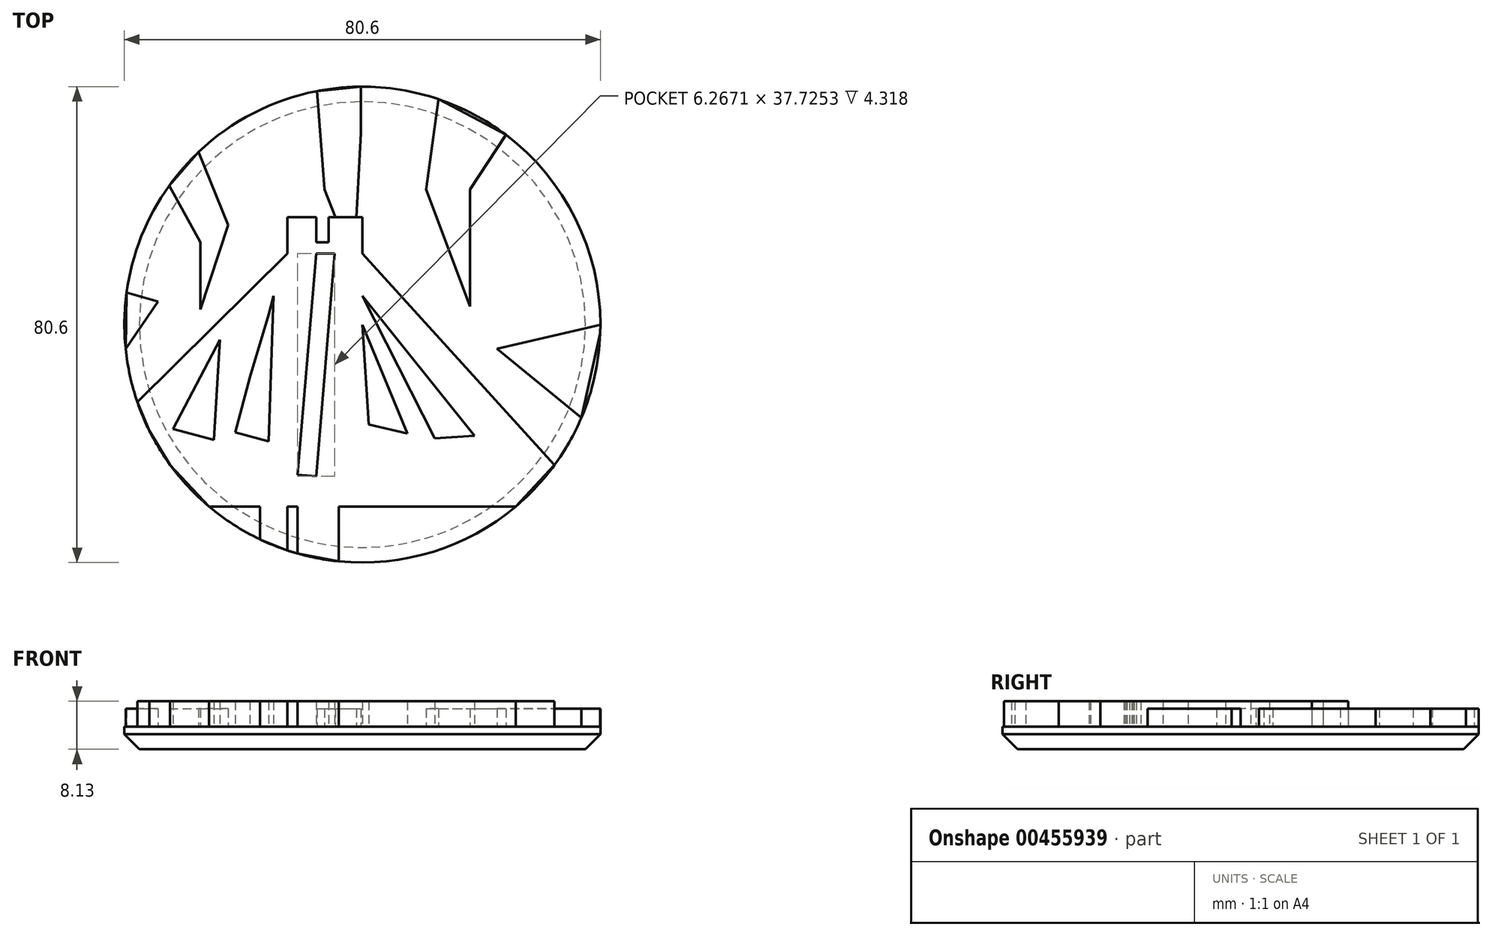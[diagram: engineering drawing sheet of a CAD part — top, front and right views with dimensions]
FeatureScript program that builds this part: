
annotation { "Feature Type Name" : "Feature", "Feature Type Description" : "" }
export const myFeature = defineFeature(function(context is Context, id is Id, definition is map)
    precondition{}
    {
        {
            var Q0;
            Q0=qCreatedBy(makeId("Top.planeOp"),FACE);
            var sketch = newSketch(context, id + "F0", { "sketchPlane" : qUnion([Q0])});
            skCircle(sketch, "E0", {"center": v(0, 0) * mm, "radius": 40.3 * mm});
            skSolve(sketch);
        }
        {
            var Q0;
            Q0=makeQuery(id+"F0.imprint","IMPRINT",FACE,{"disambiguationData":[TD([[makeQuery(id+"F0.imprint","IMPRINT",EDGE,{"derivedFrom":sQuery(id+"F0.wireOp",EDGE,"E0")}),1.0]])]});
            extrude(context, id + "F1", {"entities" : qUnion([Q0]), "depth" : 3.8 * mm});
        }
        {
            var Q0;
            Q0=makeQuery(id+"F1.opExtrude","CAP_FACE",FACE,{"disambiguationData":[OSD([sQuery(id+"F0.wireOp",EDGE,"E0")])],"isStart":false});
            var sketch = newSketch(context, id + "F2", { "sketchPlane" : qUnion([Q0])});
            skLineSegment(sketch, "E1", {"start": v(-38.1, -13.14) * mm, "end": v(-12.7, 12.07) * mm});
            skLineSegment(sketch, "E2", {"start": v(-12.7, 12.07) * mm, "end": v(-12.7, 18.2) * mm});
            skLineSegment(sketch, "E3", {"start": v(-12.7, 18.2) * mm, "end": v(-7.83, 18.2) * mm});
            skLineSegment(sketch, "E4", {"start": v(-7.83, 18.2) * mm, "end": v(-7.83, 13.97) * mm});
            skLineSegment(sketch, "E5", {"start": v(-7.83, 13.97) * mm, "end": v(-5.72, 13.97) * mm});
            skLineSegment(sketch, "E6", {"start": v(-5.72, 13.97) * mm, "end": v(-5.72, 18.2) * mm});
            skLineSegment(sketch, "E7", {"start": v(-5.72, 18.2) * mm, "end": v(0, 18.2) * mm});
            skLineSegment(sketch, "E8", {"start": v(0, 18.2) * mm, "end": v(0, 12.07) * mm});
            skLineSegment(sketch, "E9", {"start": v(0, 12.07) * mm, "end": v(32.55, -23.77) * mm});
            skLineSegment(sketch, "E10", {"start": v(32.55, -23.77) * mm, "end": v(25.97, -30.82) * mm});
            skLineSegment(sketch, "E11", {"start": v(25.97, -30.82) * mm, "end": v(-4.02, -30.82) * mm});
            skLineSegment(sketch, "E12", {"start": v(-4.02, -30.82) * mm, "end": v(-4.02, -40.1) * mm});
            skLineSegment(sketch, "E13", {"start": v(-4.02, -40.1) * mm, "end": v(-10.95, -38.78) * mm});
            skLineSegment(sketch, "E14", {"start": v(-10.95, -38.78) * mm, "end": v(-10.95, -30.82) * mm});
            skLineSegment(sketch, "E15", {"start": v(-10.95, -30.82) * mm, "end": v(-12.7, -30.82) * mm});
            skLineSegment(sketch, "E16", {"start": v(-12.7, -30.82) * mm, "end": v(-12.7, -38.25) * mm});
            skLineSegment(sketch, "E17", {"start": v(-12.7, -38.25) * mm, "end": v(-17.34, -36.38) * mm});
            skLineSegment(sketch, "E18", {"start": v(-17.34, -36.38) * mm, "end": v(-17.34, -30.82) * mm});
            skLineSegment(sketch, "E19", {"start": v(-17.34, -30.82) * mm, "end": v(-25.97, -30.82) * mm});
            skLineSegment(sketch, "E20", {"start": v(-25.97, -30.82) * mm, "end": v(-32.55, -23.77) * mm});
            skLineSegment(sketch, "E21", {"start": v(-32.55, -23.77) * mm, "end": v(-36.05, -18.02) * mm});
            skLineSegment(sketch, "E22", {"start": v(-36.05, -18.02) * mm, "end": v(-38.1, -13.14) * mm});
            skLineSegment(sketch, "E23", {"start": v(-4.02, -23.77) * mm, "end": v(25.97, -27.3) * mm});
            skLineSegment(sketch, "E24", {"start": v(26.25, -27.3) * mm, "end": v(26.25, -21.8) * mm});
            skLineSegment(sketch, "E25", {"start": v(26.25, -21.8) * mm, "end": v(-4.02, -23.77) * mm});
            skLineSegment(sketch, "E26", {"start": v(0, 4.87) * mm, "end": v(12.28, -19.26) * mm});
            skLineSegment(sketch, "E27", {"start": v(12.28, -19.26) * mm, "end": v(18.98, -18.83) * mm});
            skLineSegment(sketch, "E28", {"start": v(18.98, -18.83) * mm, "end": v(0, 4.87) * mm});
            skLineSegment(sketch, "E29", {"start": v(0, 0) * mm, "end": v(1.1, -16.89) * mm});
            skLineSegment(sketch, "E30", {"start": v(1.1, -16.89) * mm, "end": v(7.62, -18.42) * mm});
            skLineSegment(sketch, "E31", {"start": v(7.62, -18.42) * mm, "end": v(0, 0) * mm});
            skLineSegment(sketch, "E32", {"start": v(-7.83, 12.07) * mm, "end": v(-10.95, -25.4) * mm});
            skLineSegment(sketch, "E33", {"start": v(-10.95, -25.4) * mm, "end": v(-7.83, -25.66) * mm});
            skLineSegment(sketch, "E34", {"start": v(-7.83, -25.66) * mm, "end": v(-4.69, 12.07) * mm});
            skLineSegment(sketch, "E35", {"start": v(-4.69, 12.07) * mm, "end": v(-7.83, 12.07) * mm});
            skLineSegment(sketch, "E36", {"start": v(-15.03, 4.87) * mm, "end": v(-15.88, 1.7) * mm});
            skLineSegment(sketch, "E37", {"start": v(-15.88, 1.7) * mm, "end": v(-19.05, -8.9) * mm});
            skLineSegment(sketch, "E38", {"start": v(-19.05, -8.9) * mm, "end": v(-21.54, -18.23) * mm});
            skLineSegment(sketch, "E39", {"start": v(-21.54, -18.23) * mm, "end": v(-15.88, -19.74) * mm});
            skLineSegment(sketch, "E40", {"start": v(-15.88, -19.74) * mm, "end": v(-15.03, 4.87) * mm});
            skLineSegment(sketch, "E41", {"start": v(-24.13, -2.54) * mm, "end": v(-32.38, -18.23) * mm});
            skLineSegment(sketch, "E42", {"start": v(-32.38, -17.57) * mm, "end": v(-24.24, -19.74) * mm});
            skLineSegment(sketch, "E43", {"start": v(-25.19, -19.69) * mm, "end": v(-24.13, -2.54) * mm});
            skSolve(sketch);
        }
        {
            var Q0;
            Q0 = qSketchRegion(id + "F2", true);
            extrude(context, id + "F3", {"entities" : qUnion([Q0]), "operationType" : NewBodyOperationType.ADD, "depth" : 4.32 * mm});
        }
        {
            var Q0;
            {var subQ0=sQuery(id+"F0.wireOp",EDGE,"E0");var subQ1=makeQuery(id+"F1.opExtrude","CAP_FACE",FACE,{"disambiguationData":[OSD([subQ0])],"isStart":false});Q0=makeQuery(id+"F3.boolean.opBoolean","SPLIT",FACE,{"disambiguationData":[TD([makeQuery(id+"F1.opExtrude","SWEPT_FACE",FACE,{"disambiguationData":[OSD([subQ0])]}),subQ1,makeQuery(id+"F3.opExtrude","SWEPT_FACE",FACE,{"disambiguationData":[OSD([sQuery(id+"F2.wireOp",EDGE,"E1")])]}),makeQuery(id+"F3.opExtrude","SWEPT_FACE",FACE,{"disambiguationData":[OSD([sQuery(id+"F2.wireOp",EDGE,"E2")])]}),makeQuery(id+"F3.opExtrude","SWEPT_FACE",FACE,{"disambiguationData":[OSD([sQuery(id+"F2.wireOp",EDGE,"E3")])]}),makeQuery(id+"F3.opExtrude","SWEPT_FACE",FACE,{"disambiguationData":[OSD([sQuery(id+"F2.wireOp",EDGE,"E4")])]}),makeQuery(id+"F3.opExtrude","SWEPT_FACE",FACE,{"disambiguationData":[OSD([sQuery(id+"F2.wireOp",EDGE,"E5")])]}),makeQuery(id+"F3.opExtrude","SWEPT_FACE",FACE,{"disambiguationData":[OSD([sQuery(id+"F2.wireOp",EDGE,"E6")])]}),makeQuery(id+"F3.opExtrude","SWEPT_FACE",FACE,{"disambiguationData":[OSD([sQuery(id+"F2.wireOp",EDGE,"E7")])]}),makeQuery(id+"F3.opExtrude","SWEPT_FACE",FACE,{"disambiguationData":[OSD([sQuery(id+"F2.wireOp",EDGE,"E8")])]}),makeQuery(id+"F3.opExtrude","SWEPT_FACE",FACE,{"disambiguationData":[OSD([sQuery(id+"F2.wireOp",EDGE,"E9")])]}),makeQuery(id+"F3.opExtrude","SWEPT_FACE",FACE,{"disambiguationData":[OSD([sQuery(id+"F2.wireOp",EDGE,"E10")])]}),makeQuery(id+"F3.opExtrude","SWEPT_FACE",FACE,{"disambiguationData":[OSD([sQuery(id+"F2.wireOp",EDGE,"E22")])]})])],"derivedFrom":subQ1});}
            var sketch = newSketch(context, id + "F4", { "sketchPlane" : qUnion([Q0])});
            skLineSegment(sketch, "E44", {"start": v(-32.73, 23.52) * mm, "end": v(-27.42, 13.94) * mm});
            skLineSegment(sketch, "E45", {"start": v(-27.42, 13.94) * mm, "end": v(-27.42, 2.6) * mm});
            skLineSegment(sketch, "E46", {"start": v(-27.42, 2.6) * mm, "end": v(-22.7, 16.88) * mm});
            skLineSegment(sketch, "E47", {"start": v(-22.7, 16.88) * mm, "end": v(-27.75, 29.22) * mm});
            skLineSegment(sketch, "E48", {"start": v(-7.7, 39.56) * mm, "end": v(-6.38, 22.87) * mm});
            skLineSegment(sketch, "E49", {"start": v(-6.38, 22.87) * mm, "end": v(-4.6, 18.2) * mm});
            skLineSegment(sketch, "E50", {"start": v(-4.6, 18.2) * mm, "end": v(-1.03, 18.2) * mm});
            skLineSegment(sketch, "E51", {"start": v(-1.03, 18.2) * mm, "end": v(-0.26, 32.43) * mm});
            skLineSegment(sketch, "E52", {"start": v(-0.26, 32.43) * mm, "end": v(-0.26, 40.3) * mm});
            skLineSegment(sketch, "E53", {"start": v(12.91, 38.17) * mm, "end": v(10.83, 22.87) * mm});
            skLineSegment(sketch, "E54", {"start": v(10.83, 22.87) * mm, "end": v(18.23, 3.1) * mm});
            skLineSegment(sketch, "E55", {"start": v(18.23, 3.1) * mm, "end": v(18.23, 22.87) * mm});
            skLineSegment(sketch, "E56", {"start": v(18.23, 22.87) * mm, "end": v(24.3, 32.15) * mm});
            skLineSegment(sketch, "E57", {"start": v(-32.73, 23.52) * mm, "end": v(-27.75, 29.22) * mm});
            skLineSegment(sketch, "E58", {"start": v(-7.7, 39.56) * mm, "end": v(-0.26, 40.3) * mm});
            skLineSegment(sketch, "E59", {"start": v(12.91, 38.17) * mm, "end": v(24.3, 32.15) * mm});
            skLineSegment(sketch, "E60", {"start": v(-39.93, 5.46) * mm, "end": v(-34.63, 3.94) * mm});
            skLineSegment(sketch, "E61", {"start": v(-34.63, 3.94) * mm, "end": v(-40.1, -4.08) * mm});
            skLineSegment(sketch, "E62", {"start": v(-39.93, 5.46) * mm, "end": v(-40.1, -4.08) * mm});
            skLineSegment(sketch, "E63", {"start": v(40.3, 0) * mm, "end": v(22.8, -4.08) * mm});
            skLineSegment(sketch, "E64", {"start": v(22.8, -4.08) * mm, "end": v(37.1, -15.75) * mm});
            skLineSegment(sketch, "E65", {"start": v(37.1, -15.75) * mm, "end": v(40.27, -1.5) * mm});
            skLineSegment(sketch, "E66", {"start": v(40.27, -1.5) * mm, "end": v(40.3, 0) * mm});
            skSolve(sketch);
        }
        {
            var Q0;
            Q0 = qSketchRegion(id + "F4", true);
            extrude(context, id + "F5", {"entities" : qUnion([Q0]), "operationType" : NewBodyOperationType.ADD, "depth" : 3.05 * mm});
        }
        {
            var Q0;
            Q0=makeQuery(id+"F1.opExtrude","CAP_EDGE",EDGE,{"disambiguationData":[OSD([sQuery(id+"F0.wireOp",EDGE,"E0")])],"isStart":true});
            chamfer(context, id + "F6", {"entities" : qUnion([Q0]), "width" : 2.54 * mm, "tangentPropagation" : true});
        }
    });
